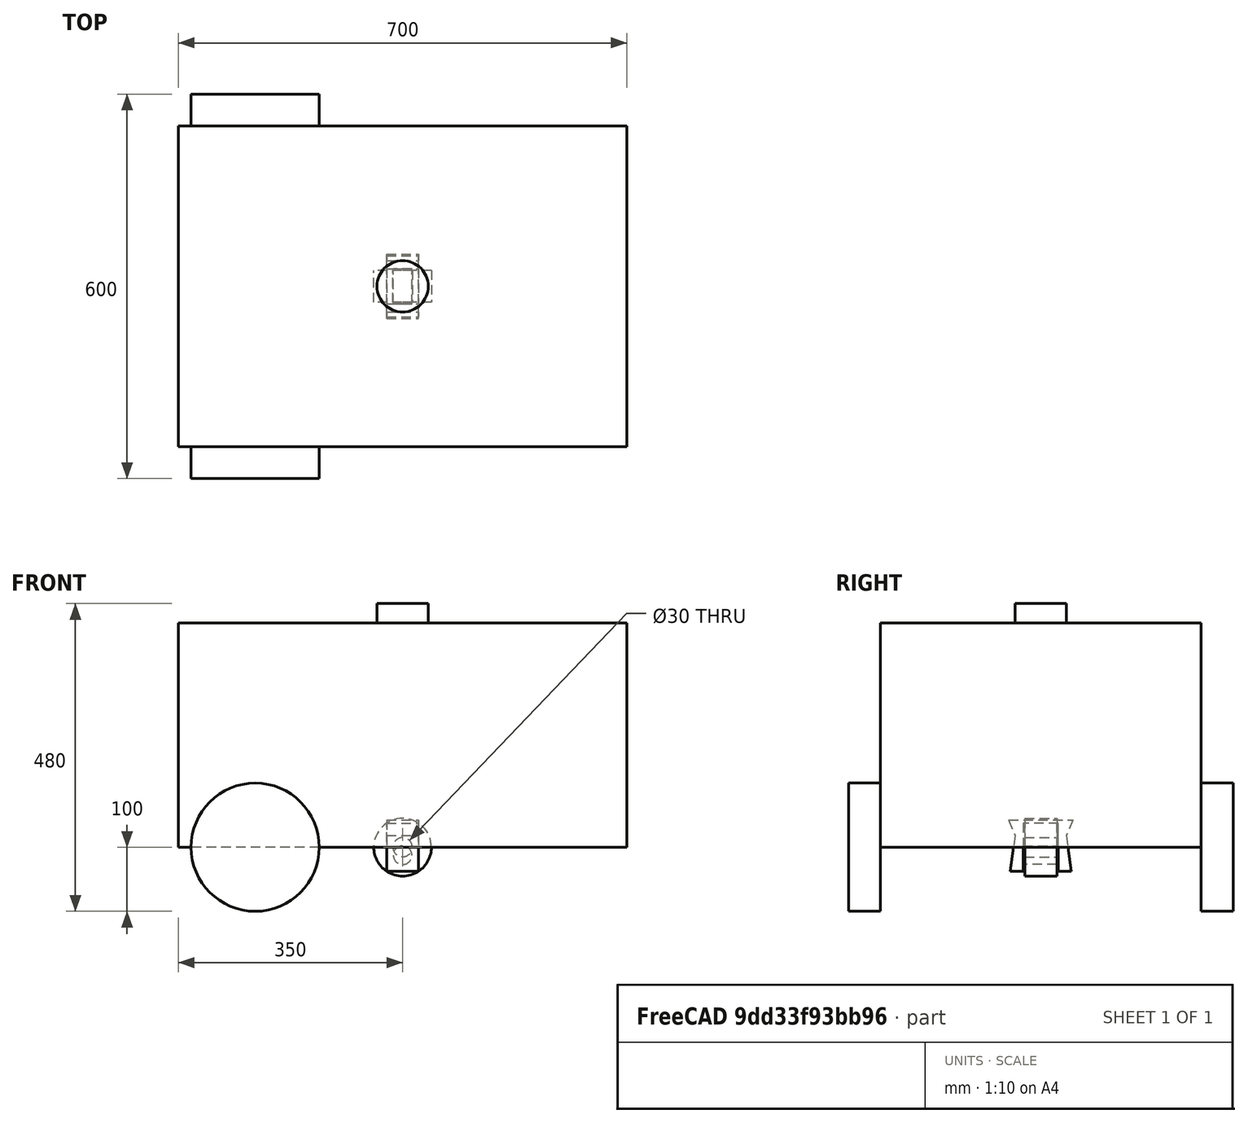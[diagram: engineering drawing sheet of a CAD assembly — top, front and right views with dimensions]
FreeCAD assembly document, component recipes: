
FREECAD ASSEMBLY — COMPONENT RECIPES ("platypous")

This assembly document has 3 components, labeled P0..P2 below (a component is one placed body or linked part). 3 of them carry a construction recipe — the FreeCAD feature program that regenerates the part from scratch, quoted from this document or its linked companion documents; the rest are supplied as boundary geometry only. No exploded tour is included for this assembly.
COMPONENT P0 — recipe-attached ("Platy-part", modeled in this document).
Construction recipe (the document's own serialized feature program — sketch geometry with constraints, then the solid features built on it; lengths are millimeters unless a unit is written):

FEATURE [Sketcher::SketchObject] Sketch
  FullyConstrained = true
  MapMode = 5
  Support = -> [XY_Plane]
  sketch-geometry (4):
    g0: LineSegment StartX=-350 StartY=250 StartZ=0 EndX=350 EndY=250 EndZ=0
    g1: LineSegment StartX=350 StartY=250 StartZ=0 EndX=350 EndY=-250 EndZ=0
    g2: LineSegment StartX=350 StartY=-250 StartZ=0 EndX=-350 EndY=-250 EndZ=0
    g3: LineSegment StartX=-350 StartY=-250 StartZ=0 EndX=-350 EndY=250 EndZ=0
  constraints (11):
    c: Coincident(g0,g1)
    c: Coincident(g1,g2)
    c: Coincident(g2,g3)
    c: Coincident(g3,g0)
    c: Horizontal(g0)
    c: Horizontal(g2)
    c: Vertical(g1)
    c: Vertical(g3)
    c: Symmetric(g0,g1,g-1)
    c: DistanceX(g2,g2) = 700
    c: DistanceY(g1,g1) = 500
FEATURE [PartDesign::Pad] Pad
  Direction = (1,1,1)
  Length = 350
  Length2 = 100
  Profile = -> Sketch
  Refine = true
  Type = 0
FEATURE [Sketcher::SketchObject] Sketch001
  FullyConstrained = true
  MapMode = 5
  Placement = pos=(0,0,350) rot=(0,0,1;0rad)
  Support = -> [Pad]
  sketch-geometry (1):
    g0: Circle CenterX=0 CenterY=0 CenterZ=0 NormalX=0 NormalY=0 NormalZ=1 AngleXU=0 Radius=40
  constraints (2):
    c: Coincident(g0,g-1)
    c: Radius(g0) = 40
FEATURE [PartDesign::Pad] Pad001
  BaseFeature = -> Pad
  Direction = (1,1,1)
  Length = 30
  Length2 = 100
  Profile = -> Sketch001
  Refine = true
  Type = 0
FEATURE [Sketcher::SketchObject] Sketch002
  ExternalGeometry = -> [Pad001]
  FullyConstrained = true
  MapMode = 5
  Placement = pos=(0,-250,0) rot=(1,0,0;1.5708rad)
  Support = -> [Pad001]
  sketch-geometry (1):
    g0: Circle CenterX=-230 CenterY=0 CenterZ=0 NormalX=0 NormalY=0 NormalZ=1 AngleXU=0 Radius=100
  constraints (3):
    c: PointOnObject(g0,g-3)
    c: Radius(g0) = 100
    c: DistanceX(g0,g-1) = 230
FEATURE [PartDesign::Pad] Pad002
  BaseFeature = -> Pad001
  Direction = (1,1,1)
  Length = 50
  Length2 = 100
  Profile = -> Sketch002
  Refine = true
  Type = 0
FEATURE [PartDesign::Mirrored] Mirrored
  BaseFeature = -> Pad002
  MirrorPlane = -> XZ_Plane
  Originals = -> [Pad002]
  Refine = true
FEATURE [PartDesign::Body] Body  label="Plataypus"
  Group = -> [Sketch,Pad,Sketch001,Pad001,Sketch002,Pad002,Mirrored]
  Origin = -> Origin
  Tip = -> Mirrored
COMPONENT P1 — recipe-attached ("Wheel", modeled in this document).
Construction recipe (the document's own serialized feature program — sketch geometry with constraints, then the solid features built on it; lengths are millimeters unless a unit is written):

FEATURE [Sketcher::SketchObject] Sketch003
  FullyConstrained = true
  MapMode = 5
  Placement = pos=(0,0,0) rot=(1,0,0;1.5708rad)
  Support = -> [XZ_Plane003]
  sketch-geometry (2):
    g0: Circle CenterX=0 CenterY=0 CenterZ=0 NormalX=0 NormalY=0 NormalZ=1 AngleXU=0 Radius=45
    g1: Circle CenterX=0 CenterY=0 CenterZ=0 NormalX=0 NormalY=0 NormalZ=1 AngleXU=0 Radius=15
  constraints (4):
    c: Coincident(g0,g-1)
    c: Radius(g0) = 45
    c: Coincident(g1,g0)
    c: Radius(g1) = 15
FEATURE [PartDesign::Pad] Pad003
  Direction = (1,1,1)
  Length = 50
  Length2 = 100
  Midplane = true
  Placement = pos=(0,0,0) rot=(1,0,0;1.5708rad)
  Profile = -> Sketch003
  Refine = true
  Type = 0
FEATURE [PartDesign::Body] Body001  label="Wheel-body"
  Group = -> [Sketch003,Pad003]
  Origin = -> Origin003
  Tip = -> Pad003
COMPONENT P2 — recipe-attached ("Wheel_Holder", modeled in this document).
Construction recipe (the document's own serialized feature program — sketch geometry with constraints, then the solid features built on it; lengths are millimeters unless a unit is written):

FEATURE [PartDesign::CoordinateSystem] LCS_0001
  AttacherType = Attacher::AttachEngine3D
  MapMode = 2
  Support = -> [X_Axis005]
FEATURE [Sketcher::SketchObject] Sketch004
  FullyConstrained = true
  MapMode = 5
  Placement = pos=(0,0,0) rot=(0.57735,0.57735,0.57735;2.0944rad)
  Support = -> [YZ_Plane005]
  sketch-geometry (10):
    g0: LineSegment StartX=-50 StartY=42.5 StartZ=0 EndX=50 EndY=42.5 EndZ=0
    g1: LineSegment StartX=27.5 StartY=-37.5 StartZ=0 EndX=47.5 EndY=-37.5 EndZ=0
    g2: LineSegment StartX=27.5 StartY=-37.5 StartZ=0 EndX=27.5 EndY=37.5 EndZ=0
    g3: LineSegment StartX=27.5 StartY=37.5 StartZ=0 EndX=-27.5 EndY=37.5 EndZ=0
    g4: LineSegment StartX=-27.5 StartY=37.5 StartZ=0 EndX=-27.5 EndY=-37.5 EndZ=0
    g5: LineSegment StartX=50 StartY=42.5 StartZ=0 EndX=40 EndY=18.1465 EndZ=0
    g6: LineSegment StartX=40 StartY=18.1465 StartZ=0 EndX=47.5 EndY=-37.5 EndZ=0
    g7: LineSegment StartX=-50 StartY=42.5 StartZ=0 EndX=-40 EndY=18.1465 EndZ=0
    g8: LineSegment StartX=-40 StartY=18.1465 StartZ=0 EndX=-47.5 EndY=-37.5 EndZ=0
    g9: LineSegment StartX=-47.5 StartY=-37.5 StartZ=0 EndX=-27.5 EndY=-37.5 EndZ=0
  constraints (28):
    c: Horizontal(g1)
    c: DistanceY(g1,g0) = 80
    c: Coincident(g1,g2)
    c: Vertical(g2)
    c: Coincident(g2,g3)
    c: Horizontal(g3)
    c: Coincident(g3,g4)
    c: Vertical(g4)
    c: Equal(g4,g2)
    c: DistanceY(g4,g4) = 75
    c: DistanceX(g3,g3) = 55
    c: Coincident(g5,g0)
    c: Coincident(g6,g5)
    c: Coincident(g6,g1)
    c: Coincident(g0,g7)
    c: Coincident(g7,g8)
    c: Coincident(g8,g9)
    c: Coincident(g9,g4)
    c: Horizontal(g9)
    c: Equal(g9,g1)
    c: Angle(g7,g8) = 2.61799
    c: Angle(g6,g5) = 2.61799
    c: Symmetric(g2,g4,g-1)
    c: DistanceX(g0,g0) = 100
    c: DistanceX(g1,g1) = 20
    c: Symmetric(g0,g0,g-2)
    c: Equal(g8,g6)
    c: DistanceX(g7,g-1) = 40
FEATURE [PartDesign::Pad] Pad004
  Direction = (1,1,1)
  Length = 50
  Length2 = 100
  Midplane = true
  Placement = pos=(0,0,0) rot=(0.57735,0.57735,0.57735;2.0944rad)
  Profile = -> Sketch004
  Refine = true
  Type = 0
FEATURE [Sketcher::SketchObject] Sketch005
  ExternalGeometry = -> [Pad004]
  FullyConstrained = true
  MapMode = 5
  Placement = pos=(1.22e-14,27.5,-9.2e-15) rot=(-0.57735,-0.57735,0.57735;4.18879rad)
  Support = -> [Pad004]
  sketch-geometry (1):
    g0: Circle CenterX=12.5 CenterY=0 CenterZ=0 NormalX=0 NormalY=0 NormalZ=1 AngleXU=0 Radius=14.5
  constraints (3):
    c: PointOnObject(g0,g-1)
    c: Radius(g0) = 14.5
    c: Distance(g0,g-3) = 50
FEATURE [PartDesign::Pad] Pad005
  BaseFeature = -> Pad004
  Direction = (1,1,1)
  Length = 10
  Length2 = 100
  Placement = pos=(0,0,0) rot=(0.57735,0.57735,0.57735;2.0944rad)
  Profile = -> Sketch005
  Refine = true
  Type = 2
FEATURE [PartDesign::Body] Wheel_holder
  Group = -> [LCS_0001,Sketch004,Pad004,Sketch005,Pad005]
  Origin = -> Origin005
  Tip = -> Pad005
PROVENANCE & LICENSES
A FreeCAD (.FCStd) document from a public repository crawl; recipes are the document's own serialized feature recipes (and, for linked parts, companion documents' recipes).
License: as declared in the source repository (recorded in the dataset sidecar).
